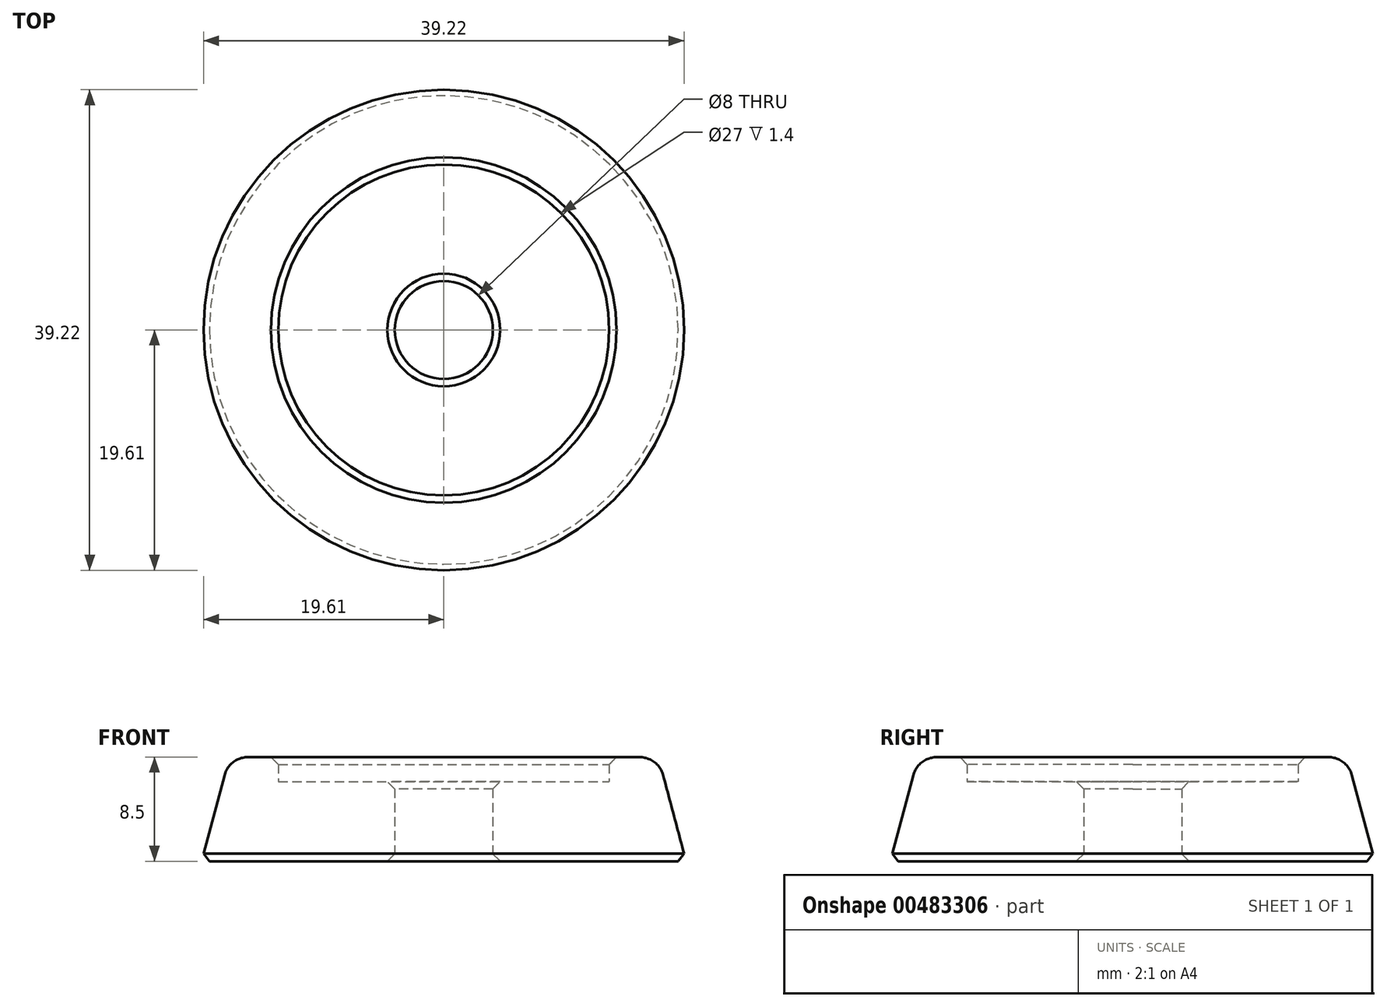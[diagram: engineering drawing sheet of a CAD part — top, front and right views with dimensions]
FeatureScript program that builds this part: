
annotation { "Feature Type Name" : "Feature", "Feature Type Description" : "" }
export const myFeature = defineFeature(function(context is Context, id is Id, definition is map)
    precondition{}
    {
        {
            var Q0;
            Q0=qCreatedBy(makeId("Front.planeOp"),FACE);
            var sketch = newSketch(context, id + "F0", { "sketchPlane" : qUnion([Q0])});
            skLineSegment(sketch, "E0", {"start": v(4, 0) * mm, "end": v(19.78, 0) * mm});
            skLineSegment(sketch, "E1", {"start": v(19.78, 0) * mm, "end": v(17.5, 8.5) * mm});
            skLineSegment(sketch, "E2", {"start": v(17.5, 8.5) * mm, "end": v(13.5, 8.5) * mm});
            skLineSegment(sketch, "E3", {"start": v(13.5, 8.5) * mm, "end": v(13.5, 6.5) * mm});
            skLineSegment(sketch, "E4", {"start": v(13.5, 6.5) * mm, "end": v(4, 6.5) * mm});
            skLineSegment(sketch, "E5", {"start": v(4, 6.5) * mm, "end": v(4, 0) * mm});
            skLineSegment(sketch, "E6", {"start": v(0, 0) * mm, "end": v(0, 4.48) * mm, "construction": true});
            skSolve(sketch);
        }
        {
            var Q0;
            Q0 = qSketchRegion(id + "F0", true);
            var Q1;
            Q1=sQuery(id+"F0.wireOp",EDGE,"E6");
            revolve(context, id + "F1", {"entities" : qUnion([Q0]), "axis" : qUnion([Q1]), "revolveType" : RevolveType.FULL});
        }
        {
            var Q0;
            Q0=makeQuery(id+"F1.opRevolve","SWEPT_EDGE",EDGE,{"disambiguationData":[OSD([sQuery(id+"F0.wireOp",EDGE,"E2"),sQuery(id+"F0.wireOp",EDGE,"E3")])]});
            var Q1;
            Q1=makeQuery(id+"F1.opRevolve","SWEPT_EDGE",EDGE,{"disambiguationData":[OSD([sQuery(id+"F0.wireOp",EDGE,"E4"),sQuery(id+"F0.wireOp",EDGE,"E5")])]});
            var Q2;
            Q2=makeQuery(id+"F1.opRevolve","SWEPT_EDGE",EDGE,{"disambiguationData":[OSD([sQuery(id+"F0.wireOp",EDGE,"E0"),sQuery(id+"F0.wireOp",EDGE,"E5")])]});
            chamfer(context, id + "F2", {"entities" : qUnion([Q0, Q1, Q2]), "width" : 0.6 * mm, "tangentPropagation" : true});
        }
        {
            var Q0;
            Q0=makeQuery(id+"F1.opRevolve","SWEPT_EDGE",EDGE,{"disambiguationData":[OSD([sQuery(id+"F0.wireOp",EDGE,"E1"),sQuery(id+"F0.wireOp",EDGE,"E2")])]});
            fillet(context, id + "F3", {"entities" : qUnion([Q0]), "radius" : 2 * mm, "tangentPropagation" : true, "allowEdgeOverflow" : false});
        }
        {
            var Q0;
            Q0=makeQuery(id+"F1.opRevolve","SWEPT_EDGE",EDGE,{"disambiguationData":[OSD([sQuery(id+"F0.wireOp",EDGE,"E0"),sQuery(id+"F0.wireOp",EDGE,"E1")])]});
            chamfer(context, id + "F4", {"entities" : qUnion([Q0]), "width" : 0.5 * mm, "tangentPropagation" : true});
        }
    });
